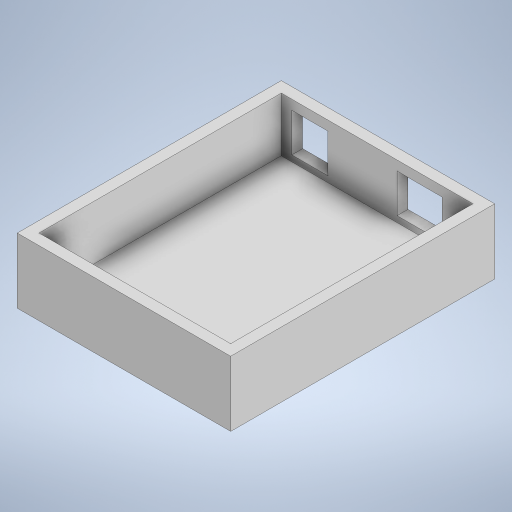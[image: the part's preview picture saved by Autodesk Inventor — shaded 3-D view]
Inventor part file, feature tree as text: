
AUTODESK INVENTOR PART (.ipt)
format: ipt  version: 2023 (Build 270158000, 158)  size: 240,640 bytes
history: native  units: in
note: dims shown in document units (in); Inventor stores cm internally (conversion verified against a paired STEP export)
features: extrude x2, sketch x2, shell x1
ambient origin geometry x8: Origin, YZ Plane, XZ Plane, XY Plane, X Axis, Y Axis, Z Axis, Center Point
bodies: Solid1 (feature_tree)
feature tree (5):
  extrude  "Extrusion1"  Depth=2.874in
  shell  "Shell1"  Thickness=0.7087in
  extrude  "Extrusion2"  Depth=0.4528in
  sketch  "Sketch2"  dims[d0=2.3228in d1=2.874in d2=0.7087in d3=0.0in]
  sketch  "Sketch3"  dims[d4=0.1181in d5=0.4528in d6=0.1831in d7=0.4921in d8=0.4213in d10=0.3937in d11=0.4213in d12=0.1831in d13=1.1811in d14=0.0in d16=1.6969in d15=0.0197in d17=0.0197in d18=0.0344in d19=0.0197in d20=0.0344in]
